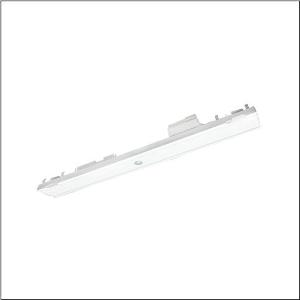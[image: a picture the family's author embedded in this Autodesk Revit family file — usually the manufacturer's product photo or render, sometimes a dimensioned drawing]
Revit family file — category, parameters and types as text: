
# Revit family: licross_r_56tl117c4x31_6d2f
name_source: partatom
category: Lighting Fixtures
units: mm (PartAtom-declared; Revit-internal decimal feet)

## family parameters
Cut with Voids When Loaded = No
Host = Face
Light Source = No
Part Type = Normal
Room Calculation Point = No
Round Connector Dimension = Use Diameter
Shared = No

## types (1)
- Licross® (1 x LED, 310 lm, 3.9 W, 4000K)
    Apparent Load = 4 VA
    CIE Flux Codes = 84 95 98 100 100
    Color Rendering = 70
    Color Temperature = 4000K
    Default Elevation = 1800 mm
    Description = Licross®, luminaire insert, of sheet steel, coil coated, white, length: 500mm, width: 59mm, height: 60mm, mounting height: 7..17m, emergency light element,LED rated luminous flux: 310lm, light colour: 740, control gear: CEAG, with plug, 6-pole, with phase selection, mains connection: 220..240V, AC/DC, 0/50..60Hz, rated input power: 3.9W, halogen-free wiring, for trunking rail, 9..14-pole, for emergency light function, supply monitoring module CEAG, with address switch, choice between two emergency light lines via tool-free moving of contact pin prior to installation in trunking rail, primary light control with lens, of PMMA, primary optical cover: cover, of PMMA, light emission: direct distribution, primary light characteristic: symmetric,  for area, compatible with all CEAG STAR technology systems (ZB-S, DG-S (DualGuard-S), LP-STAR, AT-S+), protection rating (complete): IP40, insulation class (complete): insulation class I (protective earthing), certification: CE, UKCA, protection symbol: D if used in an environment without relevant dust loads, impact resistance: IK06, permissible ambient temperature for indoor applications: -20..+40°C, packaging unit: 1 piece
    Height = 60 mm  [stored 0.19685 ft]
    Lamp = 1 x LED
    Lamp Light Flux = 310 lm
    Lamp Power = 3.9 W
    Lamp count = 1
    Length = 500 mm
    Luminous efficacy = 79 lm/W
    Manufacturer = Siteco
    ModVariant = No
    Model = 56TL117C4X31
    Mounting Place = Ceiling
    Mounting Type = Pendant
    Number of Poles = 1
    OnlyDefault = Yes
    Power Factor = 1
    Product Name = Licross®
    Product group = luminaire insert
    ProductGroupID = 901
    Protection Class = Protection class I
    Protection Degree = IP 40
    RLX_Detail_Level = 1
    RLX_Emergency_Light_Flux = 0 lm
    RLX_Emergency_Type = 0
    RLX_Emergency_Type_DB = No
    RlxData = <blob elided: 30913 chars, md5=b00b3867>
    Socket = socket
    Standby Power = 0 W
    System Light Flux = 310 lm
    System Power = 4 W
    Type Comments = Product without accessories
    Type Image = l_1251804.jpg
    URL = http://relux.com
    VarID = ---
    Voltage = 0 V
    Weight = 0.00 kg
    Width = 59 mm

note: [stored X ft] marks values corroborated as IEEE doubles in the binary element streams (Revit-internal decimal feet)

## geometry (parser evidence)
native form markers: Blend x4, Sweep x9
no freeform markers — native parametric forms only
